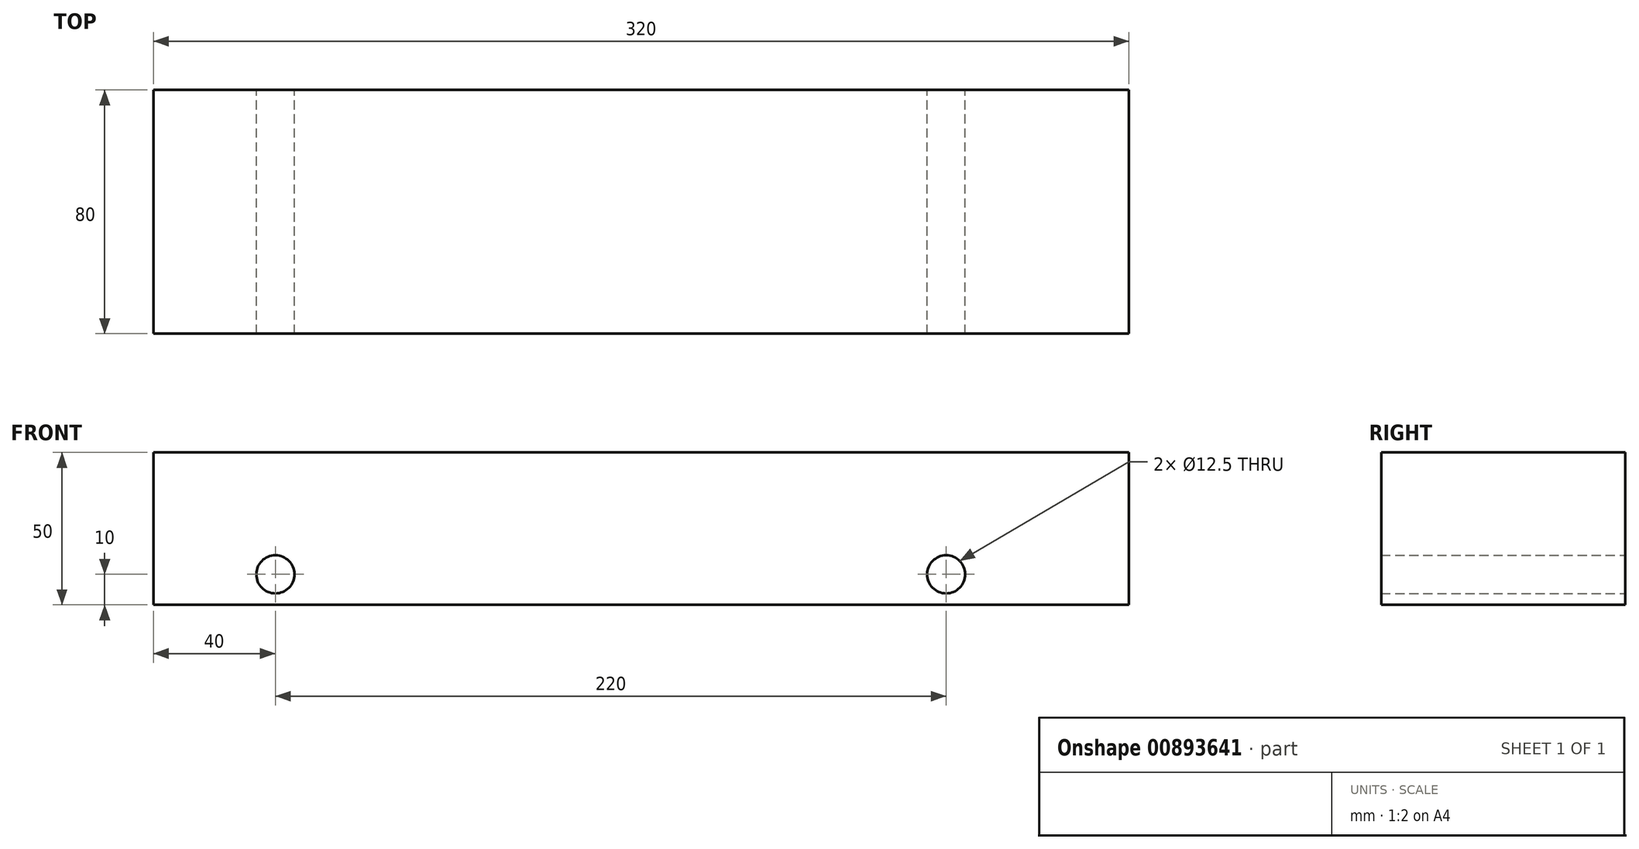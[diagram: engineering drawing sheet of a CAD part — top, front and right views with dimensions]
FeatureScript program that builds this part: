
annotation { "Feature Type Name" : "Feature", "Feature Type Description" : "" }
export const myFeature = defineFeature(function(context is Context, id is Id, definition is map)
    precondition{}
    {
        {
            var Q0;
            Q0=qCreatedBy(makeId("Front.planeOp"),FACE);
            var sketch = newSketch(context, id + "F0", { "sketchPlane" : qUnion([Q0])});
            skLineSegment(sketch, "E0.bottom", {"start": v(-160, 25) * mm, "end": v(160, 25) * mm});
            skLineSegment(sketch, "E0.top", {"start": v(-160, -25) * mm, "end": v(160, -25) * mm});
            skLineSegment(sketch, "E0.left", {"start": v(-160, 25) * mm, "end": v(-160, -25) * mm});
            skLineSegment(sketch, "E0.right", {"start": v(160, 25) * mm, "end": v(160, -25) * mm});
            skPoint(sketch, "E0.middle", {"position": v(0, 0) * mm});
            skCircle(sketch, "E1", {"center": v(-120, -15) * mm, "radius": 6.25 * mm});
            skCircle(sketch, "E2", {"center": v(100, -15) * mm, "radius": 6.25 * mm});
            skSolve(sketch);
        }
        {
            var Q0;
            Q0 = qSketchRegion(id + "F0", true);
            extrude(context, id + "F1", {"entities" : qUnion([Q0]), "endBound" : BoundingType.SYMMETRIC, "depth" : 80 * mm, "offsetDistance" : 25 * mm});
        }
    });
